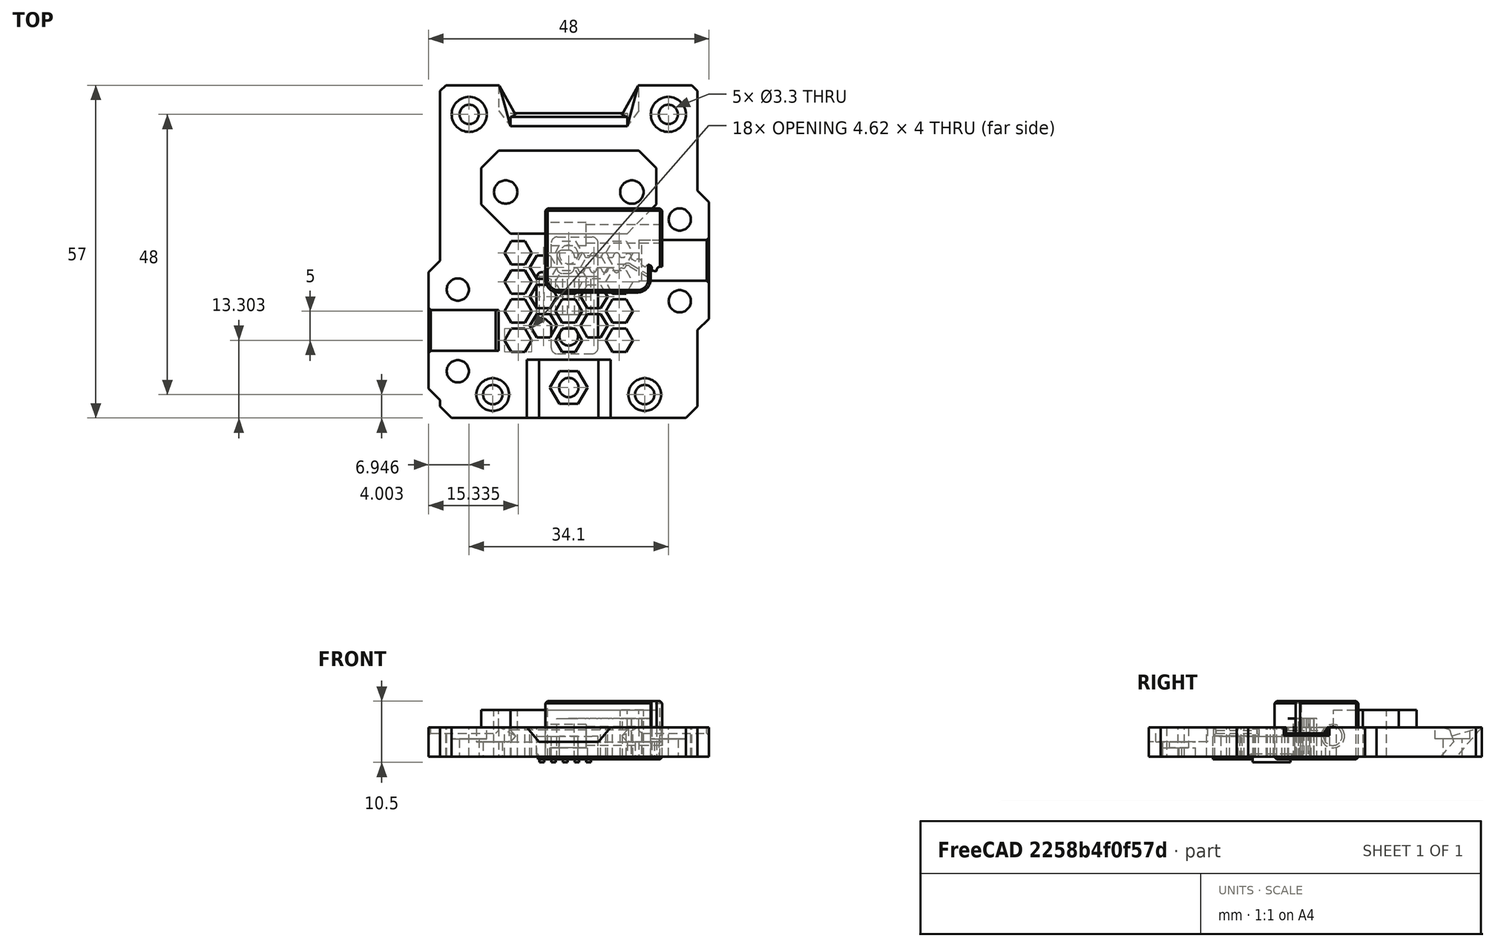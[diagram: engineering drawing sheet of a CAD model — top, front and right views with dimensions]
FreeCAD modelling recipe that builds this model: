
FCSTD DOCUMENT  (FreeCAD 0.19R24291 (Git))
Label: mounting-plate
License: Other
LicenseURL: GPL3
objects: Part::Box×22, Part::MultiFuse×18, Part::Cut×15, Part::Cylinder×14, Part::Feature×8, Part::Chamfer×7, Part::Fillet×3, Part::Extrusion×1, Part::MultiCommon×1, Part::Refine×1
note: 90 computed .brp shape members not serialized (recipe doc carries the construction recipe); baked Part::Feature solids carry a one-line shape summary decoded from their .brp

FEATURE [Part::Cylinder] Cylinder011
  Angle = 360
  AttacherType = Attacher::AttachEngine3D
  Height = 10
  Placement = pos=(0,7,0) rot=(0,0,1;0rad)
  Radius = 1.6
FEATURE [Part::Cylinder] Cylinder012
  Angle = 360
  AttacherType = Attacher::AttachEngine3D
  Height = 10
  Placement = pos=(0,-7,0) rot=(0,0,1;0rad)
  Radius = 1.6
FEATURE [Part::Box] Box008  label="Cube008"
  AttacherType = Attacher::AttachEngine3D
  Height = 4
  Length = 8
  Placement = pos=(-3,-10,0) rot=(0,0,1;0rad)
  Width = 20
FEATURE [Part::MultiFuse] Fusion017
  Shapes = -> [Cylinder011,Cylinder012]
FEATURE [Part::Fillet] Fillet002
  Base = -> Box008
  Edges = 4 edges r=1: [Edge1,Edge3,Edge5,Edge7]
FEATURE [Part::Cut] Cut008004003012001003001009
  Base = -> Fillet002
  Tool = -> Fusion017
FEATURE [Part::Cylinder] Cylinder023
  Angle = 360
  AttacherType = Attacher::AttachEngine3D
  Height = 10
  Placement = pos=(10.8,17.705,0) rot=(0,0,1;0rad)
  Radius = 2
FEATURE [Part::Cylinder] Cylinder024
  Angle = 360
  AttacherType = Attacher::AttachEngine3D
  Height = 10
  Placement = pos=(-19,1,0) rot=(0,0,1;0rad)
  Radius = 1.9
FEATURE [Part::Box] Box029  label="Cube025"
  AttacherType = Attacher::AttachEngine3D
  Height = 5
  Length = 3
  Placement = pos=(21,-6,0.5) rot=(0,0,1;0rad)
  Width = 24
FEATURE [Part::Chamfer] Chamfer008004
  Base = -> Box029
  Edges = 2 edges r=2: [Edge5,Edge7]
FEATURE [Part::Feature] Body008
  Placement = pos=(26,0,0) rot=(0,0,1;0rad)
  shape: bbox 5.6 x 5.6 x 10 mm, 3 faces (baked)
FEATURE [Part::Cylinder] Cylinder025
  Angle = 360
  AttacherType = Attacher::AttachEngine3D
  Height = 1
  Placement = pos=(0,-15.8,2) rot=(0,0,1;0rad)
  Radius = 4
FEATURE [Part::Cylinder] Cylinder026
  Angle = 360
  AttacherType = Attacher::AttachEngine3D
  Height = 1
  Placement = pos=(0,-15.8,2) rot=(0,0,1;0rad)
  Radius = 1.65
FEATURE [Part::Cut] Cut008004003012001003001010001014
  Base = -> Cylinder025
  Tool = -> Cylinder026
FEATURE [Part::Box] Box030  label="Cube026"
  AttacherType = Attacher::AttachEngine3D
  Height = 10
  Length = 26
  Placement = pos=(-13,27,0) rot=(0,0,1;0rad)
  Width = 10
FEATURE [Part::Box] Box031  label="Cube027"
  AttacherType = Attacher::AttachEngine3D
  Height = 2.5
  Length = 12
  Placement = pos=(12,5,4.5) rot=(0,0,1;0rad)
  Width = 7
FEATURE [Part::Cylinder] Cylinder027
  Angle = 360
  AttacherType = Attacher::AttachEngine3D
  Height = 10
  Placement = pos=(19,-1,0) rot=(0,0,1;0rad)
  Radius = 1.9
FEATURE [Part::Box] Box032  label="Cube028"
  AttacherType = Attacher::AttachEngine3D
  Height = 10
  Length = 15
  Placement = pos=(-7.5,-21,2.5) rot=(0,0,1;0rad)
  Width = 11
FEATURE [Part::Cylinder] Cylinder028
  Angle = 360
  AttacherType = Attacher::AttachEngine3D
  Height = 10
  Placement = pos=(-10.8,17.71,0) rot=(0,0,1;1.5708rad)
  Radius = 2
FEATURE [Part::MultiFuse] Fusion001007011039
  Shapes = -> [Cylinder023,Cylinder028]
FEATURE [Part::Feature] Part__Feature077  label="universal_face003"
  Placement = pos=(-0.00422634,7.50353,0.50127) rot=(-1,0,0;1.5708rad)
  shape: bbox 44.11 x 57.01 x 8.01 mm, 258 faces (baked)
FEATURE [Part::Feature] Part__Feature074_cs002
  shape: bbox 30 x 14.2 x 3e-07 mm, 0 faces, 0 solids (baked)
FEATURE [Part::Extrusion] Extrude003002002
  Base = -> Part__Feature074_cs002
  Dir = (0,0,1)
  DirMode = 2
  FaceMakerClass = Part::FaceMakerBullseye
  LengthFwd = 3
  LengthRev = 0
  Placement = pos=(0,0,-1) rot=(0,0,1;0rad)
  Solid = true
  Symmetric = false
FEATURE [Part::Box] Box033  label="Cube029"
  AttacherType = Attacher::AttachEngine3D
  Height = 2.5
  Length = 12
  Placement = pos=(-24,-7,4.5) rot=(0,0,1;0rad)
  Width = 7
FEATURE [Part::MultiFuse] Fusion001007011041
  Shapes = -> [Box033,Box031]
FEATURE [Part::Chamfer] Chamfer008006
  Base = -> Fusion001007011041
  Edges = 2 edges r=0.5: [Edge8,Edge16]
  Placement = pos=(0,-2.5,0) rot=(0,0,1;0rad)
FEATURE [Part::Box] Box034  label="Cube030"
  AttacherType = Attacher::AttachEngine3D
  Height = 10
  Length = 26
  Placement = pos=(-13,27,0) rot=(0,0,1;0rad)
  Width = 10
FEATURE [Part::Feature] Body009  label="base-plate001"
  shape: bbox 44.1 x 57 x 5 mm, 134 faces (baked)
FEATURE [Part::MultiFuse] Fusion001007011035
  Shapes = -> [Extrude003002002,Body009]
FEATURE [Part::Feature] Part__Feature078  label="universal_face004"
  Placement = pos=(-0.00422634,7.50353,0.50127) rot=(-1,0,0;1.5708rad)
  shape: bbox 44.11 x 57.01 x 8.01 mm, 258 faces (baked)
FEATURE [Part::Cut] Cut008004003012001003001010001015
  Base = -> Box032
  Tool = -> Part__Feature078
FEATURE [Part::Cylinder] Cylinder029
  Angle = 360
  AttacherType = Attacher::AttachEngine3D
  Height = 10
  Placement = pos=(17.05,31,3.5) rot=(0,0,1;1.5708rad)
  Radius = 3
FEATURE [Part::Cut] Cut008004003012001003001010001019
  Base = -> Fusion001007011035
  Placement = pos=(0,0,0.5) rot=(0,0,1;0rad)
  Tool = -> Fusion001007011039
FEATURE [Part::Cylinder] Cylinder030
  Angle = 360
  AttacherType = Attacher::AttachEngine3D
  Height = 10
  Placement = pos=(19,13,0) rot=(0,0,1;0rad)
  Radius = 1.9
FEATURE [Part::Cylinder] Cylinder031
  Angle = 360
  AttacherType = Attacher::AttachEngine3D
  Height = 10
  Placement = pos=(-19,-13,0) rot=(0,0,1;0rad)
  Radius = 1.9
FEATURE [Part::MultiFuse] Fusion001007011043
  Shapes = -> [Cylinder024,Cylinder030,Cylinder031,Cylinder027]
FEATURE [Part::Box] Box035  label="Cube031"
  AttacherType = Attacher::AttachEngine3D
  Height = 5
  Length = 3
  Placement = pos=(-24,-18,0.5) rot=(0,0,1;0rad)
  Width = 24
FEATURE [Part::Chamfer] Chamfer008007
  Base = -> Box035
  Edges = 2 edges r=2: [Edge1,Edge3]
FEATURE [Part::MultiFuse] Fusion001007011042
  Shapes = -> [Chamfer008007,Chamfer008004]
FEATURE [Part::MultiCommon] Common001
  Placement = pos=(0,0,-0.00126953) rot=(0,0,1;0rad)
  Shapes = -> [Part__Feature077,Box030]
FEATURE [Part::Cylinder] Cylinder032
  Angle = 360
  AttacherType = Attacher::AttachEngine3D
  Height = 10
  Placement = pos=(-17.05,31,3.5) rot=(0,0,1;1.5708rad)
  Radius = 3
FEATURE [Part::MultiFuse] Fusion001007011044
  Shapes = -> [Cylinder032,Cylinder029]
FEATURE [Part::Cut] Cut008004003012001003001010001016
  Base = -> Cut008004003012001003001010001019
  Tool = -> Fusion001007011044
FEATURE [Part::Feature] Body010
  shape: bbox 5.6 x 5.6 x 10 mm, 3 faces (baked)
FEATURE [Part::MultiFuse] Fusion001007011036
  Placement = pos=(0,0,3) rot=(0,0,1;0rad)
  Shapes = -> [Body008,Body010]
FEATURE [Part::Cut] Cut008004003012001003001010001017
  Base = -> Cut008004003012001003001010001016
  Tool = -> Fusion001007011036
FEATURE [Part::Cut] Cut008004003012001003001010001018
  Base = -> Cut008004003012001003001010001017
  Tool = -> Cut008004003012001003001010001015
FEATURE [Part::MultiFuse] Fusion001007011037
  Shapes = -> [Cut008004003012001003001010001014,Cut008004003012001003001010001018]
FEATURE [Part::Cut] Cut008004003012001003001010001020
  Base = -> Fusion001007011037
  Tool = -> Box034
FEATURE [Part::MultiFuse] Fusion001007011040
  Shapes = -> [Common001,Cut008004003012001003001010001020]
FEATURE [Part::MultiFuse] Fusion001007011045
  Shapes = -> [Fusion001007011040,Fusion001007011042]
FEATURE [Part::Cut] Cut008004003012001003001010001021
  Base = -> Fusion001007011045
  Tool = -> Fusion001007011043
FEATURE [Part::Cut] Cut008004003012001003001010001022
  Base = -> Cut008004003012001003001010001021
  Tool = -> Chamfer008006
FEATURE [Part::Chamfer] Chamfer008008  label="front-plate-2p4-base"
  Base = -> Cut008004003012001003001010001022
  Edges = 6 edges r=0.4: [Edge206,Edge213,Edge241,Edge248,Edge540,Edge556]
FEATURE [Part::Box] Box036  label="Cube032"
  AttacherType = Attacher::AttachEngine3D
  Height = 10
  Length = 20
  Placement = pos=(-4,0.5,0) rot=(0,0,1;0rad)
  Width = 14.4
FEATURE [Part::Cylinder] Cylinder033
  Angle = 360
  AttacherType = Attacher::AttachEngine3D
  Height = 7
  Placement = pos=(3,10.5,4) rot=(0.57735,-0.57735,-0.57735;2.0944rad)
  Radius = 2
FEATURE [Part::Feature] Cut008004004001  label="Cut008004005"
  shape: bbox 30 x 15.4 x 10 mm, 103 faces (baked)
FEATURE [Part::Cylinder] Cylinder034
  Angle = 360
  AttacherType = Attacher::AttachEngine3D
  Height = 24
  Placement = pos=(18,10.5,4) rot=(0.57735,-0.57735,-0.57735;2.0944rad)
  Radius = 1.6
FEATURE [Part::MultiFuse] Fusion001007002
  Shapes = -> [Cylinder034,Cylinder033]
FEATURE [Part::Box] Box037  label="Cube033"
  AttacherType = Attacher::AttachEngine3D
  Height = 10
  Length = 10
  Placement = pos=(14,-3,0) rot=(0,0,1;0rad)
  Width = 10
FEATURE [Part::Cut] Cut008004004002
  Base = -> Box037
  Placement = pos=(0,0,6) rot=(0,0,1;0rad)
  Tool = -> Cut008004004001
FEATURE [Part::Feature] Extrude001001  label="belt-cut001"
  Placement = pos=(-0.3,-1.1,-3) rot=(0,0,1;0rad)
  shape: bbox 18.15 x 13.85 x 7 mm, 84 faces (baked)
FEATURE [Part::Cut] Cut008004004003
  Base = -> Box036
  Tool = -> Extrude001001
FEATURE [Part::Cut] Cut008004004004
  Base = -> Cut008004004003
  Tool = -> Cut008004004002
FEATURE [Part::Cut] Cut008004004005
  Base = -> Cut008004004004
  Tool = -> Fusion001007002
FEATURE [Part::Refine] Cut008004004005001
  Source = -> Cut008004004005
FEATURE [Part::Fillet] Fillet010
  Base = -> Cut008004004005001
  Edges = 2 edges r=2.2: [Edge1,Edge7]
FEATURE [Part::Chamfer] Chamfer008009  label="belt-tesioner-block"
  Base = -> Fillet010
  Edges = 17 edges r=0.4: [Edge1,Edge3,Edge4,Edge6,Edge13,Edge14,Edge15,Edge16,Edge17,Edge18,Edge20,Edge21,Edge23,Edge24,Edge102,Edge103,Edge104]
FEATURE [Part::Box] Box038  label="Cube034"
  AttacherType = Attacher::AttachEngine3D
  Height = 0.5
  Length = 0.8
  Placement = pos=(-1.8,-3.25,-0.5) rot=(0,0,1;0rad)
  Width = 6.5
FEATURE [Part::Box] Box039  label="Cube035"
  AttacherType = Attacher::AttachEngine3D
  Height = 0.5
  Length = 1.2
  Placement = pos=(-3,-3.25,0) rot=(0,0,1;0rad)
  Width = 6.5
FEATURE [Part::Box] Box040  label="Cube036"
  AttacherType = Attacher::AttachEngine3D
  Height = 0.5
  Length = 0.8
  Placement = pos=(0.2,-3.25,-0.5) rot=(0,0,1;0rad)
  Width = 6.5
FEATURE [Part::Box] Box041  label="Cube037"
  AttacherType = Attacher::AttachEngine3D
  Height = 0.5
  Length = 0.8
  Placement = pos=(2.2,-3.25,-0.5) rot=(0,0,1;0rad)
  Width = 6.5
FEATURE [Part::Box] Box042  label="Cube038"
  AttacherType = Attacher::AttachEngine3D
  Height = 0.5
  Length = 0.8
  Placement = pos=(4.2,-3.25,-0.5) rot=(0,0,1;0rad)
  Width = 6.5
FEATURE [Part::Box] Box043  label="Cube039"
  AttacherType = Attacher::AttachEngine3D
  Height = 0.5
  Length = 1.2
  Placement = pos=(-1,-3.25,0) rot=(0,0,1;0rad)
  Width = 6.5
FEATURE [Part::Box] Box044  label="Cube040"
  AttacherType = Attacher::AttachEngine3D
  Height = 0.5
  Length = 1.2
  Placement = pos=(1,-3.25,0) rot=(0,0,1;0rad)
  Width = 6.5
FEATURE [Part::Box] Box045  label="Cube041"
  AttacherType = Attacher::AttachEngine3D
  Height = 0.5
  Length = 1.2
  Placement = pos=(3,-3.25,0) rot=(0,0,1;0rad)
  Width = 6.5
FEATURE [Part::MultiFuse] Fusion001007011047
  Placement = pos=(0.8,0,0) rot=(0,0,1;0rad)
  Shapes = -> [Box045,Box044,Box043,Box039]
FEATURE [Part::MultiFuse] Fusion001007011046
  Placement = pos=(-1.2,0,0) rot=(0,0,1;0rad)
  Shapes = -> [Box042,Box041,Box040,Box038]
FEATURE [Part::Box] Box046  label="Cube042"
  AttacherType = Attacher::AttachEngine3D
  Height = 4
  Length = 3
  Placement = pos=(-5.5,-4,0) rot=(0,0,1;0rad)
  Width = 8
FEATURE [Part::MultiFuse] Fusion001007011048
  Shapes = -> [Cut008004003012001003001009,Box046]
FEATURE [Part::Fillet] Fillet
  Base = -> Fusion001007011048
  Edges = 2 edges r=1: [Edge1,Edge3]
FEATURE [Part::Chamfer] Chamfer008010
  Base = -> Fillet
  Edges = 2 edges r=1: [Edge17,Edge21]
FEATURE [Part::Box] Box047  label="Cube043"
  AttacherType = Attacher::AttachEngine3D
  Height = 0.5
  Length = 0.8
  Placement = pos=(-5,-3.25,-0.5) rot=(0,0,1;0rad)
  Width = 6.5
FEATURE [Part::Box] Box048  label="Cube044"
  AttacherType = Attacher::AttachEngine3D
  Height = 0.5
  Length = 1.2
  Placement = pos=(-4.2,-3.25,0) rot=(0,0,1;0rad)
  Width = 6.5
FEATURE [Part::MultiFuse] Fusion001007011049
  Shapes = -> [Box047,Fusion001007011046]
FEATURE [Part::MultiFuse] Fusion001007011051
  Shapes = -> [Chamfer008010,Fusion001007011049]
FEATURE [Part::Box] Box049  label="Cube045"
  AttacherType = Attacher::AttachEngine3D
  Height = 0.5
  Length = 1.2
  Placement = pos=(-6.2,-3.25,0) rot=(0,0,1;0rad)
  Width = 6.5
FEATURE [Part::MultiFuse] Fusion001007011052
  Shapes = -> [Fusion001007011047,Box048,Box049]
FEATURE [Part::Cut] Cut008004003012001003001010001023
  Base = -> Fusion001007011051
  Tool = -> Fusion001007011052
FEATURE [Part::Chamfer] Chamfer008011  label="belt-clamp"
  Base = -> Cut008004003012001003001010001023
  Edges = 5 edges r=0.4: [Edge12,Edge13,Edge16,Edge18,Edge19]
